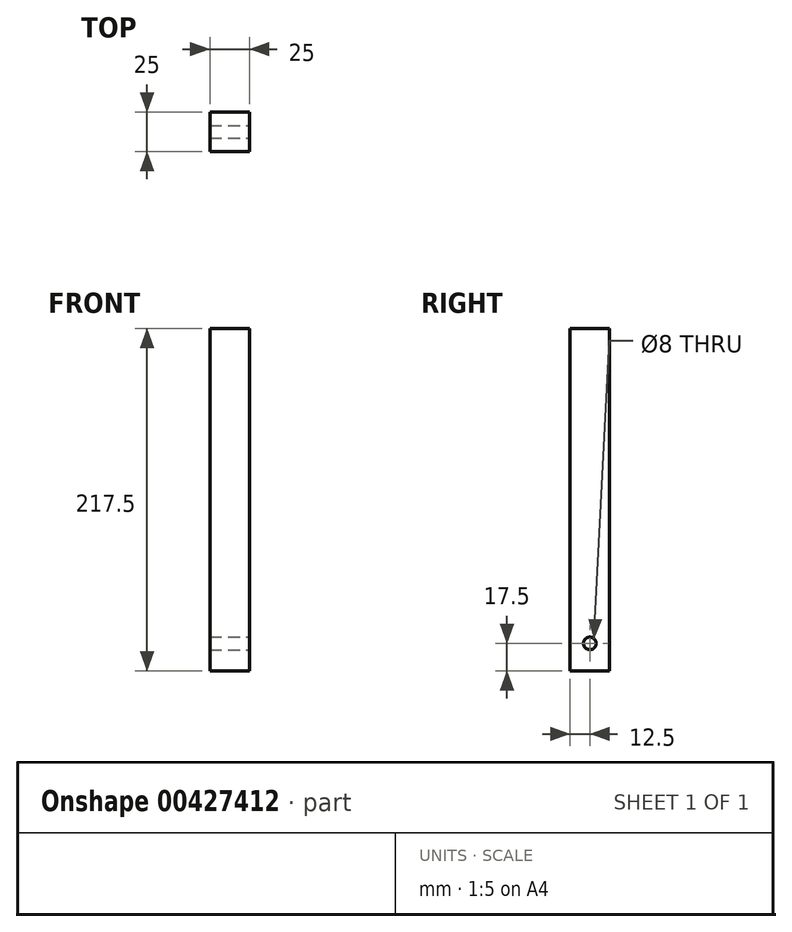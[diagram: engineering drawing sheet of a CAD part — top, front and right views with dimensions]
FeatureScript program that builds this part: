
annotation { "Feature Type Name" : "Feature", "Feature Type Description" : "" }
export const myFeature = defineFeature(function(context is Context, id is Id, definition is map)
    precondition{}
    {
        {
            var Q0;
            Q0=qCreatedBy(makeId("Front.planeOp"),FACE);
            var sketch = newSketch(context, id + "F0", { "sketchPlane" : qUnion([Q0])});
            skLineSegment(sketch, "E0.bottom", {"start": v(12.5, 108.75) * mm, "end": v(-12.5, 108.75) * mm});
            skLineSegment(sketch, "E0.top", {"start": v(12.5, -108.75) * mm, "end": v(-12.5, -108.75) * mm});
            skLineSegment(sketch, "E0.left", {"start": v(12.5, 108.75) * mm, "end": v(12.5, -108.75) * mm});
            skLineSegment(sketch, "E0.right", {"start": v(-12.5, 108.75) * mm, "end": v(-12.5, -108.75) * mm});
            skPoint(sketch, "E0.middle", {"position": v(0, 0) * mm});
            skSolve(sketch);
        }
        {
            var Q0;
            Q0=makeQuery(id+"F0.imprint","IMPRINT",FACE,{"disambiguationData":[TD([[makeQuery(id+"F0.imprint","IMPRINT",EDGE,{"derivedFrom":sQuery(id+"F0.wireOp",EDGE,"E0.bottom")}),1.0]])]});
            extrude(context, id + "F1", {"entities" : qUnion([Q0]), "depth" : 25 * mm});
        }
        {
            var Q0;
            Q0=makeQuery(id+"F1.opExtrude","SWEPT_FACE",FACE,{"disambiguationData":[OSD([sQuery(id+"F0.wireOp",EDGE,"E0.left")])]});
            var sketch = newSketch(context, id + "F2", { "sketchPlane" : qUnion([Q0])});
            skCircle(sketch, "E1", {"center": v(-12.5, -91.25) * mm, "radius": 4 * mm});
            skPoint(sketch, "E1.centerSnap0", {"position": v(-12.5, -108.75) * mm});
            skSolve(sketch);
        }
        {
            var Q0;
            Q0 = qSketchRegion(id + "F2", true);
            extrude(context, id + "F3", {"entities" : qUnion([Q0]), "operationType" : NewBodyOperationType.REMOVE, "oppositeDirection" : true, "depth" : 25 * mm});
        }
    });
